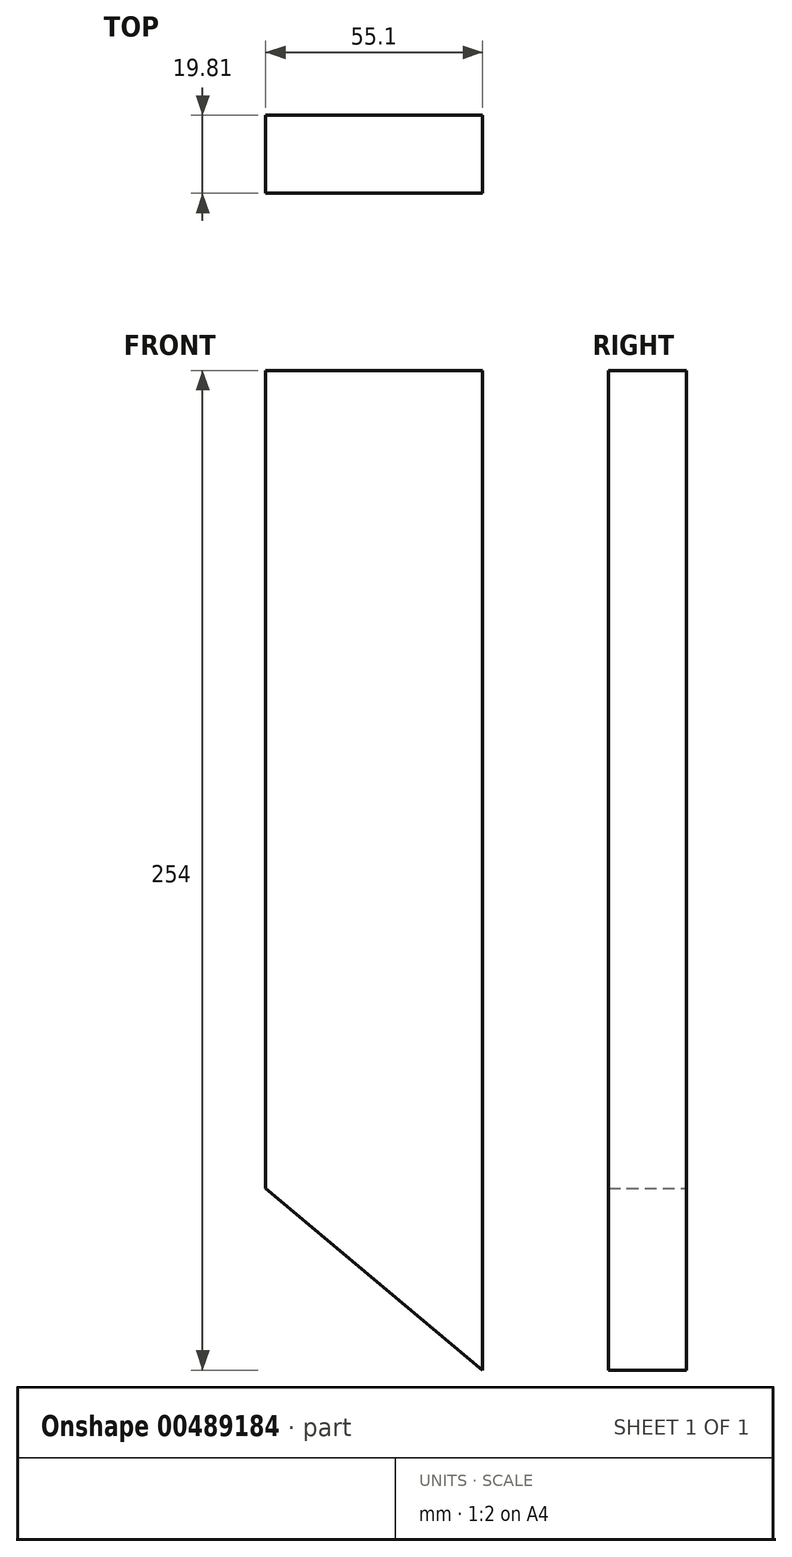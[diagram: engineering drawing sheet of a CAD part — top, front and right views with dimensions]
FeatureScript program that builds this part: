
annotation { "Feature Type Name" : "Feature", "Feature Type Description" : "" }
export const myFeature = defineFeature(function(context is Context, id is Id, definition is map)
    precondition{}
    {
        {
            var Q0;
            Q0=qCreatedBy(makeId("Front.planeOp"),FACE);
            var sketch = newSketch(context, id + "F0", { "sketchPlane" : qUnion([Q0])});
            skLineSegment(sketch, "E0.bottom", {"start": v(-36.4, 181.15) * mm, "end": v(18.7, 181.15) * mm});
            skLineSegment(sketch, "E0.top", {"start": v(-36.4, -72.85) * mm, "end": v(18.7, -72.85) * mm});
            skLineSegment(sketch, "E0.left", {"start": v(-36.4, 181.15) * mm, "end": v(-36.4, -72.85) * mm});
            skLineSegment(sketch, "E0.right", {"start": v(18.7, 181.15) * mm, "end": v(18.7, -72.85) * mm});
            skLineSegment(sketch, "E1", {"start": v(18.7, -72.85) * mm, "end": v(-36.4, -26.62) * mm});
            skSolve(sketch);
        }
        {
            var Q0;
            Q0=makeQuery(id+"F0.imprint","IMPRINT",FACE,{"disambiguationData":[TD([[makeQuery(id+"F0.imprint","IMPRINT",EDGE,{"derivedFrom":sQuery(id+"F0.wireOp",EDGE,"E0.bottom")}),-1.0]])]});
            extrude(context, id + "F1", {"entities" : qUnion([Q0]), "depth" : 19.8 * mm, "offsetDistance" : 25.4 * mm});
        }
    });
